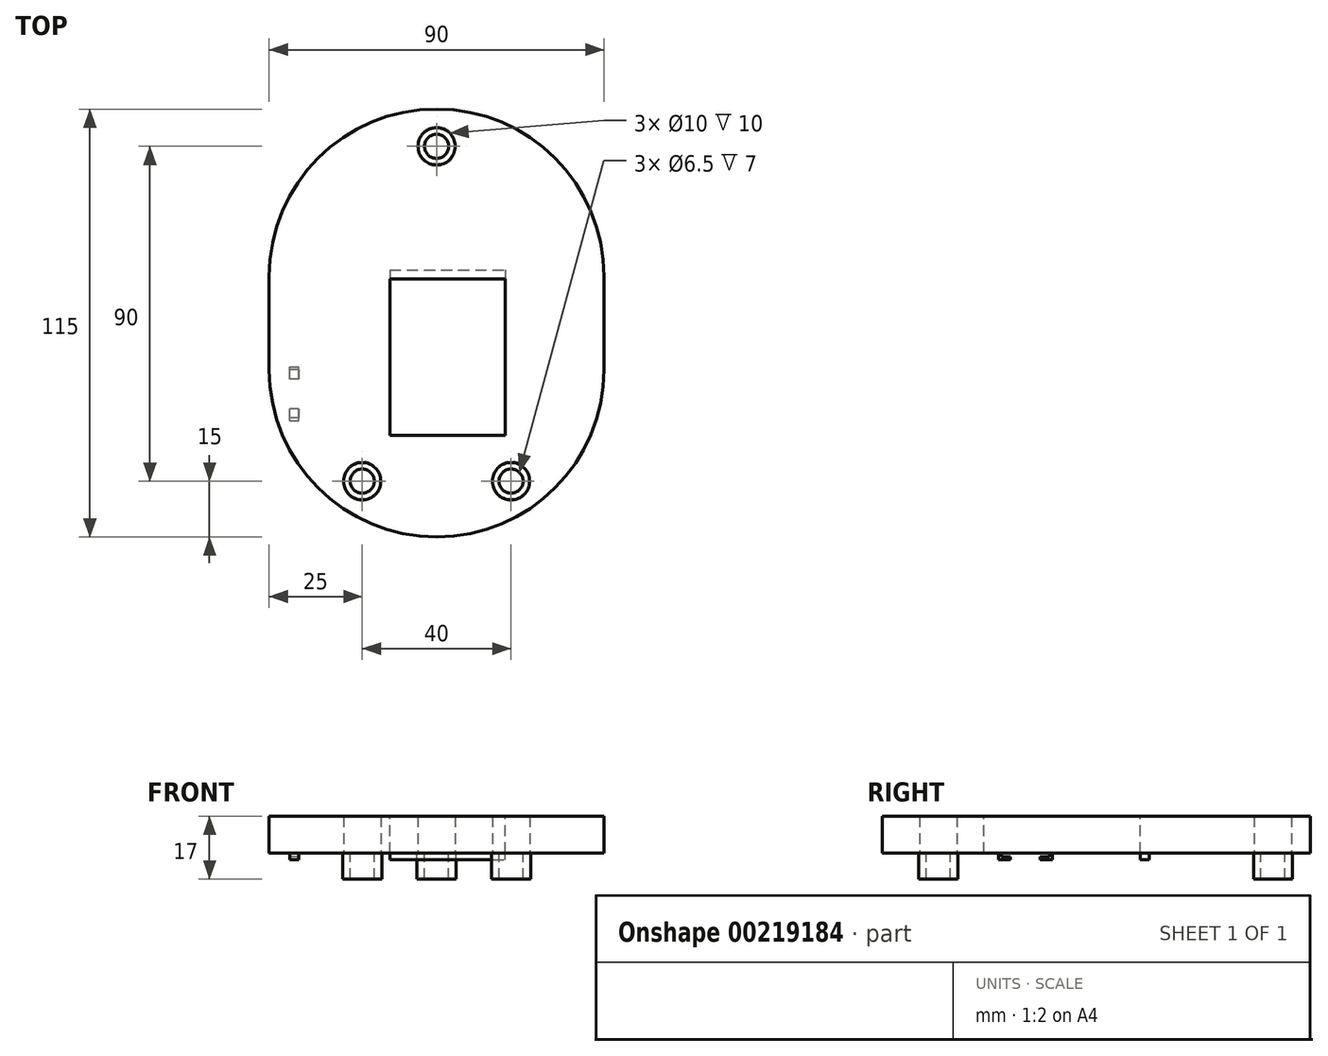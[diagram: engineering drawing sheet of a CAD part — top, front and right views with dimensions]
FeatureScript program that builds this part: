
annotation { "Feature Type Name" : "Feature", "Feature Type Description" : "" }
export const myFeature = defineFeature(function(context is Context, id is Id, definition is map)
    precondition{}
    {
        {
            var Q0;
            Q0=qCreatedBy(makeId("Top.planeOp"),FACE);
            var sketch = newSketch(context, id + "F0", { "sketchPlane" : qUnion([Q0])});
            skArc(sketch, "E0", {"start": v(-45, 0) * mm, "mid": v(0, -45) * mm, "end": v(45, 0) * mm});
            skLineSegment(sketch, "E1", {"start": v(-45, 0) * mm, "end": v(-45, 70) * mm});
            skLineSegment(sketch, "E2", {"start": v(-45, 70) * mm, "end": v(45, 70) * mm});
            skLineSegment(sketch, "E3", {"start": v(45, 70) * mm, "end": v(45, 0) * mm});
            skSolve(sketch);
        }
        {
            var Q0;
            Q0=qSketchRegion(id+"F0",true);
            extrude(context, id + "F1", {"entities" : qUnion([Q0]), "depth" : 10 * mm});
        }
        {
            var Q0;
            Q0=makeQuery(id+"F1.opExtrude","CAP_FACE",FACE,{"disambiguationData":[OSD([sQuery(id+"F0.wireOp",EDGE,"E0")])],"isStart":true});
            var sketch = newSketch(context, id + "F2", { "sketchPlane" : qUnion([Q0])});
            skCircle(sketch, "E4", {"center": v(0, 0) * mm, "radius": 9.5 * mm});
            skSolve(sketch);
        }
        {
            var Q0;
            Q0=makeQuery(id+"F1.opExtrude","SWEPT_EDGE",EDGE,{"disambiguationData":[OSD([sQuery(id+"F0.wireOp",EDGE,"E1"),sQuery(id+"F0.wireOp",EDGE,"E2")])]});
            var Q1;
            Q1=makeQuery(id+"F1.opExtrude","SWEPT_EDGE",EDGE,{"disambiguationData":[OSD([sQuery(id+"F0.wireOp",EDGE,"E2"),sQuery(id+"F0.wireOp",EDGE,"E3")])]});
            fillet(context, id + "F3", {"entities" : qUnion([Q0, Q1]), "radius" : 45 * mm, "tangentPropagation" : true, "allowEdgeOverflow" : false});
        }
        {
            var Q0;
            Q0=makeQuery(id+"F1.opExtrude","CAP_FACE",FACE,{"disambiguationData":[OSD([sQuery(id+"F0.wireOp",EDGE,"E0"),sQuery(id+"F0.wireOp",EDGE,"E1"),sQuery(id+"F0.wireOp",EDGE,"E2"),sQuery(id+"F0.wireOp",EDGE,"E3")])],"isStart":false});
            var sketch = newSketch(context, id + "F4", { "sketchPlane" : qUnion([Q0])});
            skLineSegment(sketch, "E5.bottom", {"start": v(-12.6, 24.3) * mm, "end": v(18.4, 24.3) * mm});
            skLineSegment(sketch, "E5.top", {"start": v(-12.6, -17.7) * mm, "end": v(18.4, -17.7) * mm});
            skLineSegment(sketch, "E5.left", {"start": v(-12.6, 24.3) * mm, "end": v(-12.6, -17.7) * mm});
            skLineSegment(sketch, "E5.right", {"start": v(18.4, 24.3) * mm, "end": v(18.4, -17.7) * mm});
            skSolve(sketch);
        }
        {
            var Q0;
            Q0=makeQuery(id+"F4.imprint","IMPRINT",FACE,{"disambiguationData":[TD([[makeQuery(id+"F4.imprint","IMPRINT",EDGE,{"derivedFrom":sQuery(id+"F4.wireOp",EDGE,"E5.bottom")}),-1.0]])]});
            extrude(context, id + "F5", {"entities" : qUnion([Q0]), "operationType" : NewBodyOperationType.REMOVE, "oppositeDirection" : true, "depth" : 11 * mm});
        }
        {
            var Q0;
            Q0=makeQuery(id+"F2.imprint","IMPRINT",FACE,{"disambiguationData":[TD([[makeQuery(id+"F2.imprint","IMPRINT",EDGE,{"derivedFrom":sQuery(id+"F2.wireOp",EDGE,"E4")}),-1.0]])]});
            var sketch = newSketch(context, id + "F6", { "sketchPlane" : qUnion([Q0])});
            skPoint(sketch, "E6", {"position": v(20, 30) * mm});
            skPoint(sketch, "E7", {"position": v(-20, 30) * mm});
            skPoint(sketch, "E8", {"position": v(0, -60) * mm});
            skCircle(sketch, "E9", {"center": v(0, -60) * mm, "radius": 5.25 * mm});
            skCircle(sketch, "E10", {"center": v(20, 30) * mm, "radius": 5.25 * mm});
            skCircle(sketch, "E11", {"center": v(-20, 30) * mm, "radius": 5.25 * mm});
            skSolve(sketch);
        }
        {
            var Q0;
            Q0=makeQuery(id+"F6.imprint","IMPRINT",FACE,{"disambiguationData":[TD([[makeQuery(id+"F6.imprint","IMPRINT",EDGE,{"derivedFrom":sQuery(id+"F6.wireOp",EDGE,"E9")}),1.0]])]});
            var Q1;
            Q1=makeQuery(id+"F6.imprint","IMPRINT",FACE,{"disambiguationData":[TD([[makeQuery(id+"F6.imprint","IMPRINT",EDGE,{"derivedFrom":sQuery(id+"F6.wireOp",EDGE,"E11")}),1.0]])]});
            var Q2;
            Q2=makeQuery(id+"F6.imprint","IMPRINT",FACE,{"disambiguationData":[TD([[makeQuery(id+"F6.imprint","IMPRINT",EDGE,{"derivedFrom":sQuery(id+"F6.wireOp",EDGE,"E10")}),1.0]])]});
            extrude(context, id + "F7", {"entities" : qUnion([Q0, Q1, Q2]), "operationType" : NewBodyOperationType.ADD, "depth" : 7 * mm});
        }
        {
            var Q0;
            Q0=makeQuery(id+"F1.opExtrude","CAP_FACE",FACE,{"disambiguationData":[OSD([sQuery(id+"F0.wireOp",EDGE,"E0"),sQuery(id+"F0.wireOp",EDGE,"E1"),sQuery(id+"F0.wireOp",EDGE,"E2"),sQuery(id+"F0.wireOp",EDGE,"E3")])],"isStart":true});
            var sketch = newSketch(context, id + "F8", { "sketchPlane" : qUnion([Q0])});
            skPoint(sketch, "E12", {"position": v(0, -60) * mm});
            skPoint(sketch, "E13", {"position": v(20, 30) * mm});
            skPoint(sketch, "E14", {"position": v(-20, 30) * mm});
            skCircle(sketch, "E15", {"center": v(-20, 30) * mm, "radius": 5 * mm});
            skCircle(sketch, "E16", {"center": v(20, 30) * mm, "radius": 5 * mm});
            skCircle(sketch, "E17", {"center": v(0, -60) * mm, "radius": 5 * mm});
            skSolve(sketch);
        }
        {
            var Q0;
            Q0=sQuery(id+"F8.wireOp",VERTEX,"E14");
            var Q1;
            Q1=sQuery(id+"F8.wireOp",VERTEX,"E13");
            var Q2;
            Q2=sQuery(id+"F8.wireOp",VERTEX,"E12");
            var Q3;
            Q3=makeQuery(id+"F1.opExtrude","SWEPT_BODY",BODY,{"disambiguationData":[OSD([sQuery(id+"F0.wireOp",EDGE,"E0"),sQuery(id+"F0.wireOp",EDGE,"E1"),sQuery(id+"F0.wireOp",EDGE,"E2"),sQuery(id+"F0.wireOp",EDGE,"E3")])]});
            hole(context, id + "F9", {"style" : HoleStyle.SIMPLE, "endStyle" : HoleEndStyle.THROUGH, "holeDiameter" : 10 * mm, "locations" : qUnion([Q0, Q1, Q2]), "scope" : qUnion([Q3]), "isTappedThrough" : true});
        }
        {
            var Q0;
            Q0=sQuery(id+"F8.wireOp",VERTEX,"E13");
            var Q1;
            Q1=sQuery(id+"F8.wireOp",VERTEX,"E12");
            var Q2;
            Q2=sQuery(id+"F6.wireOp",VERTEX,"E7");
            var Q3;
            Q3=makeQuery(id+"F1.opExtrude","SWEPT_BODY",BODY,{"disambiguationData":[OSD([sQuery(id+"F0.wireOp",EDGE,"E0"),sQuery(id+"F0.wireOp",EDGE,"E1"),sQuery(id+"F0.wireOp",EDGE,"E2"),sQuery(id+"F0.wireOp",EDGE,"E3")])]});
            hole(context, id + "F10", {"style" : HoleStyle.SIMPLE, "endStyle" : HoleEndStyle.THROUGH, "oppositeDirection" : true, "holeDiameter" : 6.5 * mm, "locations" : qUnion([Q0, Q1, Q2]), "scope" : qUnion([Q3]), "isTappedThrough" : true});
        }
        {
            var Q0;
            {var subQ3=sQuery(id+"F0.wireOp",EDGE,"E0");Q0=makeQuery(id+"F8.imprint","IMPRINT",FACE,{"disambiguationData":[TD([[makeQuery(id+"F8.imprint","IMPRINT",EDGE,{"derivedFrom":makeQuery(id+"F1.opExtrude","CAP_EDGE",EDGE,{"disambiguationData":[OSD([subQ3])],"isStart":true})}),-1.0]])]});}
            var sketch = newSketch(context, id + "F11", { "sketchPlane" : qUnion([Q0])});
            skLineSegment(sketch, "E18.bottom", {"start": v(-12.6, -26.8) * mm, "end": v(18.4, -26.8) * mm});
            skLineSegment(sketch, "E18.top", {"start": v(-12.6, -24.3) * mm, "end": v(18.4, -24.3) * mm});
            skLineSegment(sketch, "E18.left", {"start": v(-12.6, -26.8) * mm, "end": v(-12.6, -24.3) * mm});
            skLineSegment(sketch, "E18.right", {"start": v(18.4, -26.8) * mm, "end": v(18.4, -24.3) * mm});
            skSolve(sketch);
        }
        {
            var Q0;
            Q0=makeQuery(id+"F11.imprint","IMPRINT",FACE,{"disambiguationData":[TD([[makeQuery(id+"F11.imprint","IMPRINT",EDGE,{"derivedFrom":sQuery(id+"F11.wireOp",EDGE,"E18.bottom")}),1.0]])]});
            extrude(context, id + "F12", {"entities" : qUnion([Q0]), "operationType" : NewBodyOperationType.ADD, "depth" : 1.7 * mm});
        }
        {
            var Q0;
            {var subQ3=sQuery(id+"F0.wireOp",EDGE,"E0");Q0=makeQuery(id+"F8.imprint","IMPRINT",FACE,{"disambiguationData":[TD([[makeQuery(id+"F8.imprint","IMPRINT",EDGE,{"derivedFrom":makeQuery(id+"F1.opExtrude","CAP_EDGE",EDGE,{"disambiguationData":[OSD([subQ3])],"isStart":true})}),-1.0]])]});}
            var sketch = newSketch(context, id + "F13", { "sketchPlane" : qUnion([Q0])});
            skLineSegment(sketch, "E19.bottom", {"start": v(-39.5, 13.8) * mm, "end": v(-37, 13.8) * mm});
            skLineSegment(sketch, "E19.top", {"start": v(-39.5, -0.7) * mm, "end": v(-37, -0.7) * mm});
            skLineSegment(sketch, "E19.left", {"start": v(-39.5, 13.8) * mm, "end": v(-39.5, -0.7) * mm});
            skLineSegment(sketch, "E19.right", {"start": v(-37, 13.8) * mm, "end": v(-37, -0.7) * mm});
            skSolve(sketch);
        }
        {
            var Q0;
            Q0=makeQuery(id+"F13.imprint","IMPRINT",FACE,{"disambiguationData":[TD([[makeQuery(id+"F13.imprint","IMPRINT",EDGE,{"derivedFrom":sQuery(id+"F13.wireOp",EDGE,"E19.bottom")}),-1.0]])]});
            extrude(context, id + "F14", {"entities" : qUnion([Q0]), "operationType" : NewBodyOperationType.ADD, "depth" : 1.7 * mm});
        }
        {
            var Q0;
            Q0=makeQuery(id+"F14.opExtrude","SWEPT_FACE",FACE,{"disambiguationData":[OSD([sQuery(id+"F13.wireOp",EDGE,"E19.left")])]});
            var sketch = newSketch(context, id + "F15", { "sketchPlane" : qUnion([Q0])});
            skLineSegment(sketch, "E20.bottom", {"start": v(13, 0) * mm, "end": v(0, 0) * mm});
            skLineSegment(sketch, "E20.top", {"start": v(13, -1) * mm, "end": v(10.55, -1) * mm});
            skLineSegment(sketch, "E20.left", {"start": v(13, 0) * mm, "end": v(13, -1) * mm});
            skLineSegment(sketch, "E20.right", {"start": v(0, 0) * mm, "end": v(0, -1) * mm});
            skLineSegment(sketch, "E21.bottom", {"start": v(10.55, -1.7) * mm, "end": v(2.55, -1.7) * mm});
            skLineSegment(sketch, "E21.left", {"start": v(10.55, -1.7) * mm, "end": v(10.55, -1) * mm});
            skLineSegment(sketch, "E21.right", {"start": v(2.55, -1.7) * mm, "end": v(2.55, -1) * mm});
            skLineSegment(sketch, "E22.trimOffspring", {"start": v(2.55, -1) * mm, "end": v(0, -1) * mm});
            skSolve(sketch);
        }
        {
            var Q0;
            Q0=makeQuery(id+"F15.imprint","IMPRINT",FACE,{"disambiguationData":[TD([[makeQuery(id+"F15.imprint","IMPRINT",EDGE,{"derivedFrom":sQuery(id+"F15.wireOp",EDGE,"E20.bottom")}),1.0]])]});
            extrude(context, id + "F16", {"entities" : qUnion([Q0]), "operationType" : NewBodyOperationType.REMOVE, "oppositeDirection" : true, "depth" : 25 * mm});
        }
    });
